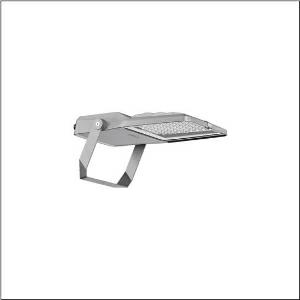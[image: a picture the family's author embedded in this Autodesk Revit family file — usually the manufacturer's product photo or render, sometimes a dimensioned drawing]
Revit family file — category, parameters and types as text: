
# Revit family: floodlight_fl_21_iq_mini___pl61_5xa7772b4c1a_1528
name_source: partatom
category: Lighting Fixtures
units: mm (PartAtom-declared; Revit-internal decimal feet)

## family parameters
Cut with Voids When Loaded = No
Host = Face
Light Source = No
Part Type = Normal
Room Calculation Point = No
Round Connector Dimension = Use Diameter
Shared = No

## types (1)
- --- (1 x LED, 6370 lm, 45.5 W, 4000K)
    Apparent Load = 46 VA
    CIE Flux Codes = 33 65 98 100 100
    Color Rendering = 70
    Color Temperature = 4000K
    Default Elevation = 1800 mm
    Description = Floodlight FL 21 iQ mini, floodlight, primary light control with lens, of PMMA, primary optical cover: protective disc, of toughened safety glass, transparent, light distribution: PL61, light emission: direct distribution, installation type: surface-mounted, lamps: LED, High Power LED, rated values: 6.370lm | 45,5W | 140lm/W (begin service life); end service life: 6.370lm | 48W; at 50% lumin. flux: 3.185lm | 21,5W | 148,1lm/W, colour temperature: 4000K, colour rendering: CRI > 70, light colour: 740, light setting 1 begin service life: 100% | 6.370lm | 45,5W | 140lm/W | 4.000K, light setting 1 end service life: 48W, further light settings possible, control: Street-Remote, Auto-Match, Temp-Guard, Night-Set, Smart-Wire, Desk-Remote (wireless, voltage-free reading and setting of iQ features in the workshop via application-optimized NFC function/RFID function), optimised constant luminous flux control (CLO 2.0), pre-setting: linear dimming characteristic, with terminal, 6-pole, mains connection: 220..240V, AC, 50/60Hz, luminaire housing, of diecast aluminium, powder-coated, SITECO metallic grey (DB 702S), corrosivity category C5 mid according to DIN EN ISO 12944suitable for swimming poolschlorine-resistant, sealing non-destructively replaceable, mounting bracket, of steel, galvanised, powder-coated, SITECO metallic grey (DB 702S), protection rating (complete): IP66, insulation class (complete): insulation class II (safety insulation), certification: CE, ENEC, VDE, protection symbol: D, impact resistance: IK08, permissible operating ambient temperature: -40..+40°C, permissible operating ambient temperature for outdoor applications: -40..+50°C, standard: DIN EN 12944, LABS conformity tested according to VDMA 24364:2018-05, packaging unit: 1 piece

Light Distribution: PL61
    Height = 70 mm
    Lamp = 1 x LED
    Lamp Light Flux = 6370 lm
    Lamp Power = 45.5 W
    Lamp count = 1
    Length = 485 mm
    Luminous efficacy = 140 lm/W
    Manufacturer = Siteco
    ModVariant = No
    Model = 5XA7772B4C1A
    Number of Poles = 1
    OnlyDefault = Yes
    Power Factor = 1
    Product Name = Floodlight FL 21 iQ mini | PL61
    Product group = floodlight | pylon annexe
    ProductGroupID = 6201
    Protection Class = Protection class II
    Protection Degree = IP 66
    RLX_Detail_Level = 1
    RLX_Emergency_Light_Flux = 0 lm
    RLX_Emergency_Type = 0
    RLX_Emergency_Type_DB = No
    RlxData = <blob elided: 96525 chars, md5=272aacbb>
    Socket = socket
    Standby Power = 0 W
    System Light Flux = 6370 lm
    System Power = 46 W
    Type Comments = factory setting: luminous flux: 100 % | dim-lin: 254 | 463 mA
    Type Image = l_1006845.jpg
    URL = http://relux.com
    VarID = @adj_172997
    Voltage = 0 V
    Weight = 0.00 kg
    Width = 337 mm

## geometry (parser evidence)
native form markers: Blend x4, Sweep x10
no freeform markers — native parametric forms only
